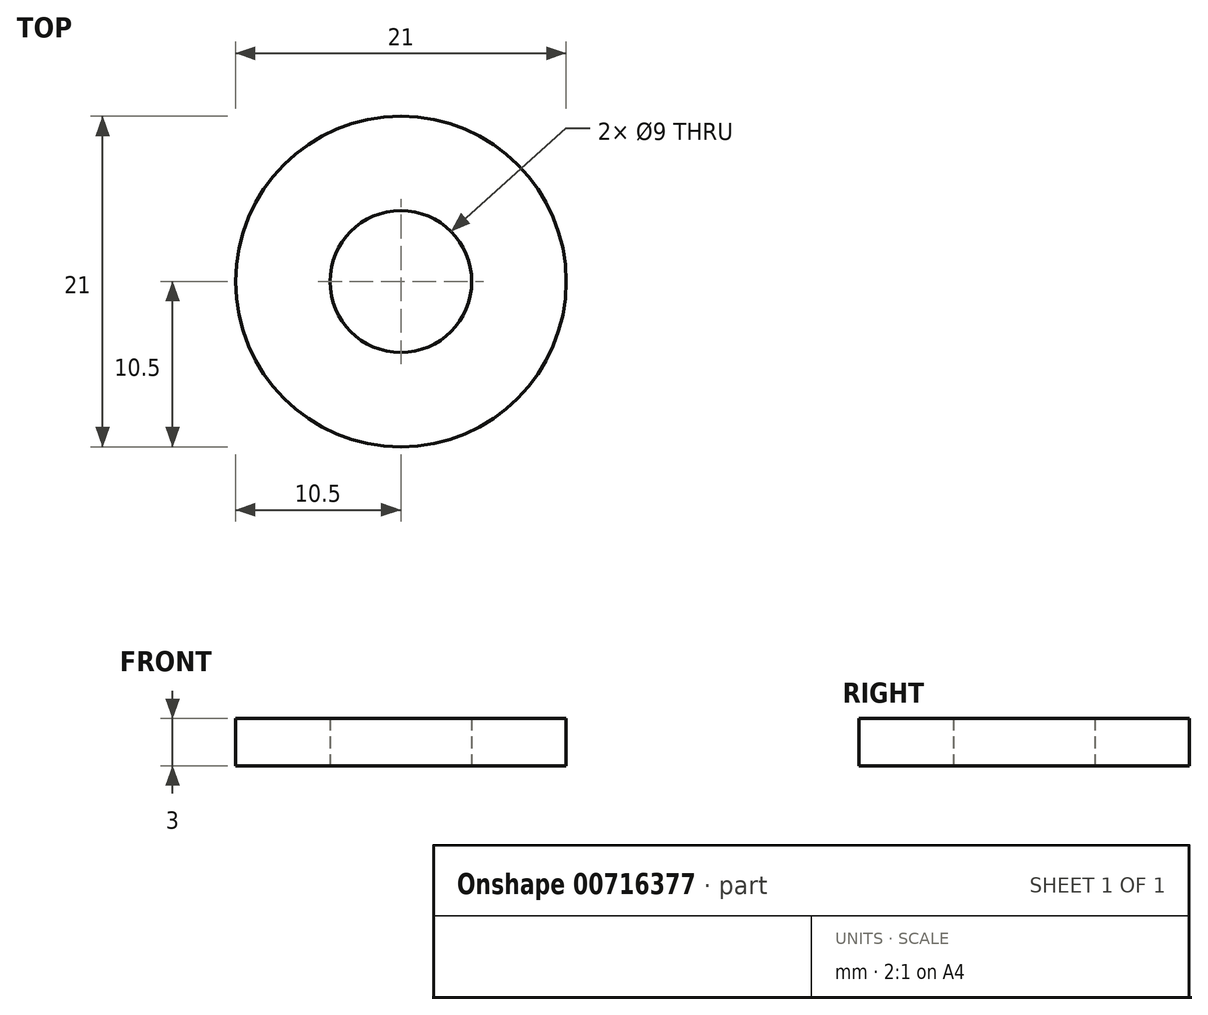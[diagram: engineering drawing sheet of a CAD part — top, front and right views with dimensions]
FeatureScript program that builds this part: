
annotation { "Feature Type Name" : "Feature", "Feature Type Description" : "" }
export const myFeature = defineFeature(function(context is Context, id is Id, definition is map)
    precondition{}
    {
        {
            var Q0;
            Q0=qCreatedBy(makeId("Top.planeOp"),FACE);
            var sketch = newSketch(context, id + "F0", { "sketchPlane" : qUnion([Q0])});
            skCircle(sketch, "E0", {"center": v(0, 0) * mm, "radius": 10.5 * mm});
            skCircle(sketch, "E1", {"center": v(0, 0) * mm, "radius": 4.5 * mm});
            skSolve(sketch);
        }
        {
            var Q0;
            Q0 = qSketchRegion(id + "F0", true);
            extrude(context, id + "F1", {"entities" : qUnion([Q0]), "depth" : 3 * mm, "offsetDistance" : 25 * mm});
        }
    });
